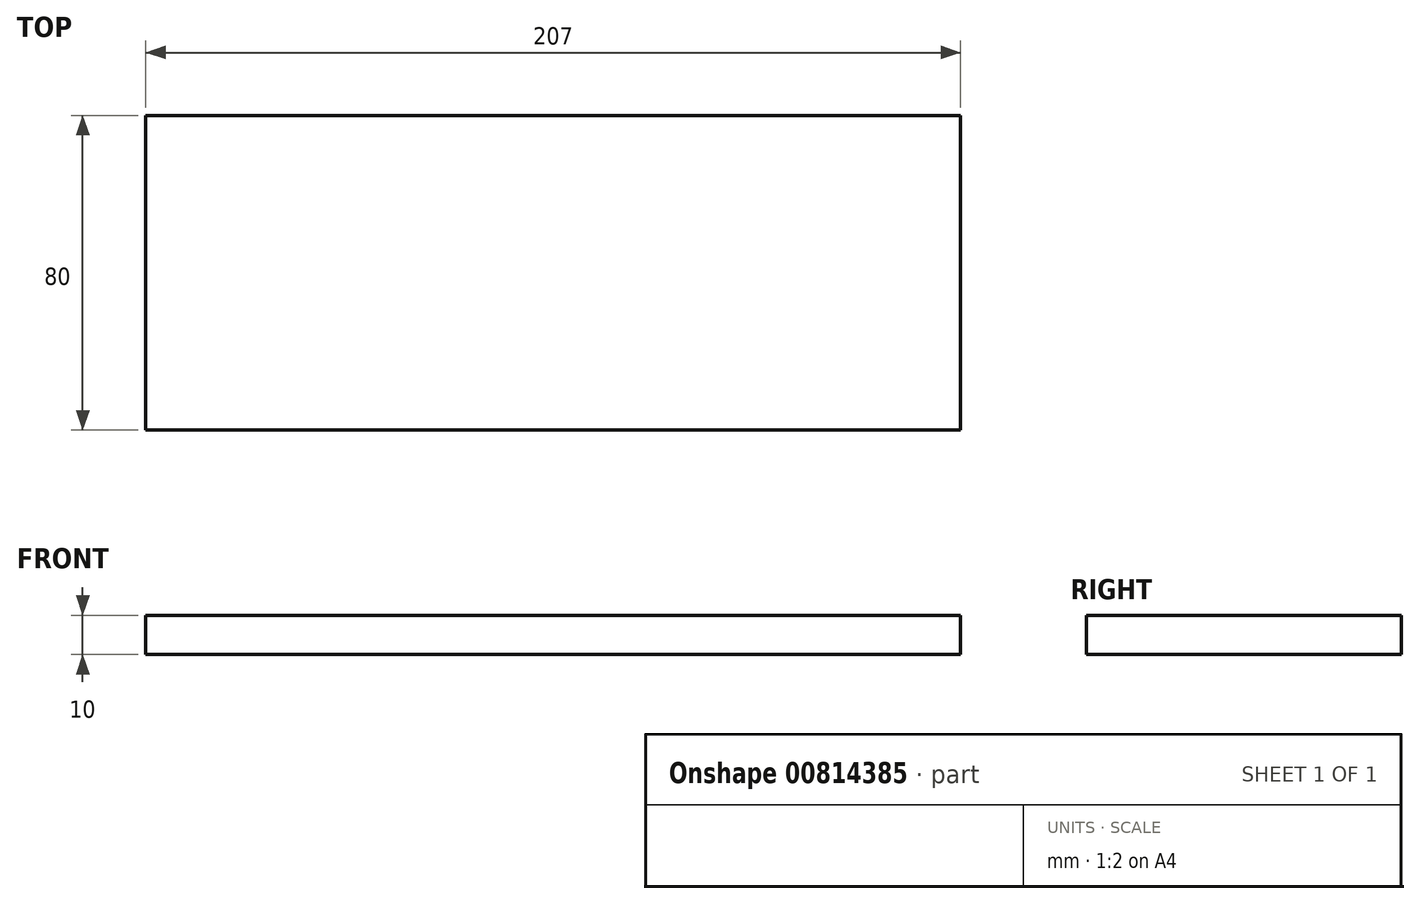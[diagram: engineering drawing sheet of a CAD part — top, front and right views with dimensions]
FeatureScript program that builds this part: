
annotation { "Feature Type Name" : "Feature", "Feature Type Description" : "" }
export const myFeature = defineFeature(function(context is Context, id is Id, definition is map)
    precondition{}
    {
        {
            var Q0;
            Q0=qCreatedBy(makeId("Top.planeOp"),FACE);
            var sketch = newSketch(context, id + "F0", { "sketchPlane" : qUnion([Q0])});
            skLineSegment(sketch, "E0.bottom", {"start": v(0, 0) * mm, "end": v(207, 0) * mm});
            skLineSegment(sketch, "E0.top", {"start": v(0, 80) * mm, "end": v(207, 80) * mm});
            skLineSegment(sketch, "E0.left", {"start": v(0, 0) * mm, "end": v(0, 80) * mm});
            skLineSegment(sketch, "E0.right", {"start": v(207, 0) * mm, "end": v(207, 80) * mm});
            skSolve(sketch);
        }
        {
            var Q0;
            Q0 = qSketchRegion(id + "F0", true);
            extrude(context, id + "F1", {"entities" : qUnion([Q0]), "depth" : 10 * mm, "offsetDistance" : 25 * mm});
        }
    });
